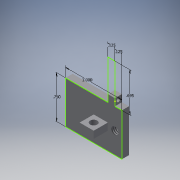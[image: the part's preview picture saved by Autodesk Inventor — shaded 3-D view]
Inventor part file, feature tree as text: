
AUTODESK INVENTOR PART (.ipt)
format: ipt  version: 2016 (Build 200138000, 138)  size: 145,920 bytes
history: native  units: in
note: dims shown in document units (in); Inventor stores cm internally (conversion verified against a paired STEP export)
features: sketch x6, hole x4, projected_geometry x3, extrude x2, thicken_offset x1
ambient origin geometry x8: Origin, YZ Plane, XZ Plane, XY Plane, X Axis, Y Axis, Z Axis, Center Point
bodies: Solid1 (feature_tree)
feature tree (16):
  extrude  "Extrusion1"  Depth=1.0in
  extrude  "Extrusion2"  Depth=0.125in
  hole  "Hole1"  [1 undecoded]
  hole  "Hole2"  [1 undecoded]
  hole  "Hole3"  [1 undecoded]
  sketch  "Sketch6"  dims[d15=0.06in d16=0.75in d17=0.375in d18=0.25in d19=0.5635in d20=1.0in d21=0.8108in d22=0.125in d23=0.125in d24=0.75in d25=0.375in d26=0.25in d27=0.5635in d28=1.0in d29=0.8108in d30=0.13in d31=0.75in d32=0.375in d33=0.25in d34=0.5635in d35=1.0in d36=0.8108in d37=0.125in d38=0.063in d39=0.063in d40=0.063in d41=0.06in d42=0.75in d43=0.375in d44=0.25in d45=0.5635in d46=1.0in d47=0.8108in d48=0.57in d49=0.57in]
  hole  "Hole4"  [1 undecoded]
  thicken_offset  "Thicken1"
  sketch  "Sketch1"  dims[d0=0.75in d2=1.0in]
  sketch  "Sketch2"  dims[d3=0.125in d4=0.695in]
  sketch  "Sketch3"  dims[d5=0.125in d6=0.0in d7=0.125in]
  projected_geometry  "Projected Loop1"
  sketch  "Sketch4"  dims[d10=0.25in d11=0.3125in]
  projected_geometry  "Projected Loop2"
  sketch  "Sketch5"  dims[d12=0.25in d13=0.25in d14=0.0in]
  projected_geometry  "Projected Loop3"
note: 4 required parameter values undecoded (feature->parameter linkage not recoverable at this tier; creation-order binding heuristic only, values carry confidence <= 0.55)
